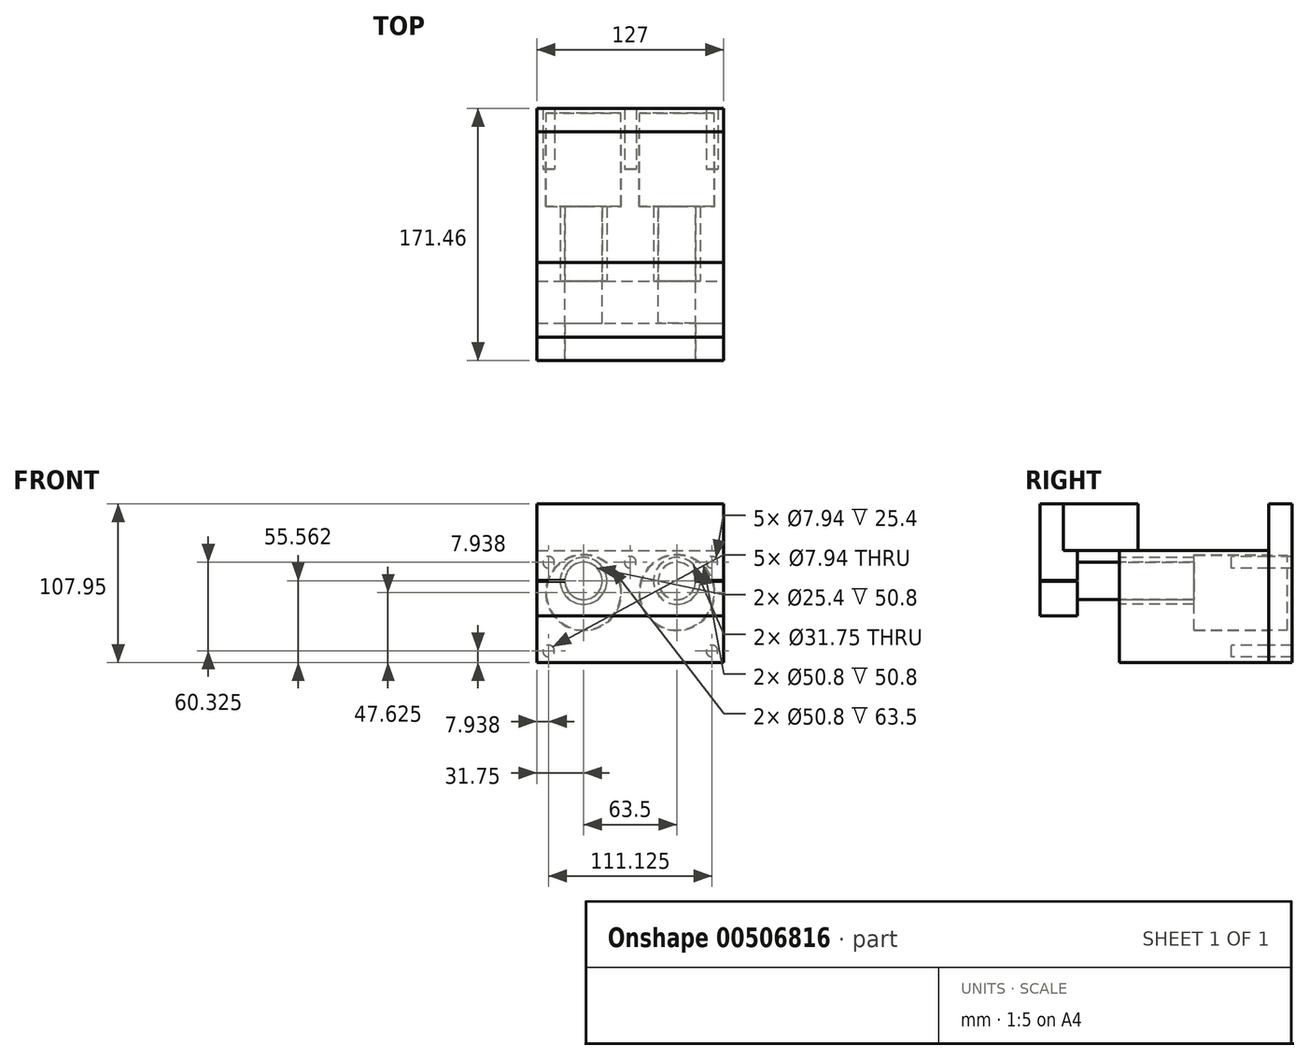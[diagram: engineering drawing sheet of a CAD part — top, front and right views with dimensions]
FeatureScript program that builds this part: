
annotation { "Feature Type Name" : "Feature", "Feature Type Description" : "" }
export const myFeature = defineFeature(function(context is Context, id is Id, definition is map)
    precondition{}
    {
        {
            var Q0;
            Q0=qCreatedBy(makeId("Front.planeOp"),FACE);
            var sketch = newSketch(context, id + "F0", { "sketchPlane" : qUnion([Q0])});
            skLineSegment(sketch, "E0.bottom", {"start": v(0, 0) * mm, "end": v(127, 0) * mm});
            skLineSegment(sketch, "E0.top", {"start": v(0, 76.2) * mm, "end": v(127, 76.2) * mm});
            skLineSegment(sketch, "E0.left", {"start": v(0, 0) * mm, "end": v(0, 76.2) * mm});
            skLineSegment(sketch, "E0.right", {"start": v(127, 0) * mm, "end": v(127, 76.2) * mm});
            skCircle(sketch, "E1", {"center": v(31.75, 47.62) * mm, "radius": 25.4 * mm});
            skCircle(sketch, "E2", {"center": v(95.25, 47.62) * mm, "radius": 25.4 * mm});
            skCircle(sketch, "E3", {"center": v(31.75, 55.56) * mm, "radius": 15.88 * mm});
            skCircle(sketch, "E4", {"center": v(95.25, 55.56) * mm, "radius": 15.88 * mm});
            skSolve(sketch);
        }
        {
            var Q0;
            Q0=makeQuery(id+"F0.imprint","IMPRINT",FACE,{"disambiguationData":[TD([[makeQuery(id+"F0.imprint","IMPRINT",EDGE,{"derivedFrom":sQuery(id+"F0.wireOp",EDGE,"E0.bottom")}),1.0]])]});
            var Q1;
            Q1=makeQuery(id+"F0.imprint","IMPRINT",FACE,{"disambiguationData":[TD([[makeQuery(id+"F0.imprint","IMPRINT",EDGE,{"derivedFrom":sQuery(id+"F0.wireOp",EDGE,"E1")}),1.0]])]});
            var Q2;
            Q2=makeQuery(id+"F0.imprint","IMPRINT",FACE,{"disambiguationData":[TD([[makeQuery(id+"F0.imprint","IMPRINT",EDGE,{"derivedFrom":sQuery(id+"F0.wireOp",EDGE,"E2")}),1.0]])]});
            extrude(context, id + "F1", {"entities" : qUnion([Q0, Q1, Q2]), "depth" : 101.6 * mm, "offsetDistance" : 25.4 * mm});
        }
        {
            var Q0;
            Q0=makeQuery(id+"F0.imprint","IMPRINT",FACE,{"disambiguationData":[TD([[makeQuery(id+"F0.imprint","IMPRINT",EDGE,{"derivedFrom":sQuery(id+"F0.wireOp",EDGE,"E1")}),1.0]])]});
            var Q1;
            Q1=makeQuery(id+"F0.imprint","IMPRINT",FACE,{"disambiguationData":[TD([[makeQuery(id+"F0.imprint","IMPRINT",EDGE,{"derivedFrom":sQuery(id+"F0.wireOp",EDGE,"E2")}),1.0]])]});
            var Q2;
            Q2=makeQuery(id+"F0.imprint","IMPRINT",FACE,{"disambiguationData":[TD([[makeQuery(id+"F0.imprint","IMPRINT",EDGE,{"derivedFrom":sQuery(id+"F0.wireOp",EDGE,"E4")}),1.0]])]});
            var Q3;
            Q3=makeQuery(id+"F0.imprint","IMPRINT",FACE,{"disambiguationData":[TD([[makeQuery(id+"F0.imprint","IMPRINT",EDGE,{"derivedFrom":sQuery(id+"F0.wireOp",EDGE,"E3")}),1.0]])]});
            extrude(context, id + "F2", {"entities" : qUnion([Q0, Q1, Q2, Q3]), "operationType" : NewBodyOperationType.REMOVE, "depth" : 50.8 * mm, "offsetDistance" : 25.4 * mm});
        }
        {
            var Q0;
            Q0=makeQuery(id+"F1.opExtrude","CAP_FACE",FACE,{"disambiguationData":[OSD([sQuery(id+"F0.wireOp",EDGE,"E0.bottom"),sQuery(id+"F0.wireOp",EDGE,"E0.top"),sQuery(id+"F0.wireOp",EDGE,"E0.left"),sQuery(id+"F0.wireOp",EDGE,"E0.right"),sQuery(id+"F0.wireOp",EDGE,"E3"),sQuery(id+"F0.wireOp",EDGE,"E4")])],"isStart":false});
            var sketch = newSketch(context, id + "F3", { "sketchPlane" : qUnion([Q0])});
            skCircle(sketch, "E5", {"center": v(31.75, 55.56) * mm, "radius": 15.88 * mm});
            skCircle(sketch, "E6", {"center": v(95.25, 55.56) * mm, "radius": 15.88 * mm});
            skCircle(sketch, "E7", {"center": v(31.75, 55.56) * mm, "radius": 12.7 * mm});
            skCircle(sketch, "E8", {"center": v(95.25, 55.56) * mm, "radius": 12.7 * mm});
            skSolve(sketch);
        }
        {
            var Q0;
            Q0 = qSketchRegion(id + "F3", true);
            extrude(context, id + "F4", {"entities" : qUnion([Q0]), "oppositeDirection" : true, "depth" : 50.8 * mm, "offsetDistance" : 25.4 * mm});
        }
        {
            var Q0;
            Q0=makeQuery(id+"F0.imprint","IMPRINT",FACE,{"disambiguationData":[TD([[makeQuery(id+"F0.imprint","IMPRINT",EDGE,{"derivedFrom":sQuery(id+"F0.wireOp",EDGE,"E0.bottom")}),1.0]])]});
            var sketch = newSketch(context, id + "F5", { "sketchPlane" : qUnion([Q0])});
            skCircle(sketch, "E9", {"center": v(95.25, 47.62) * mm, "radius": 25.4 * mm});
            skCircle(sketch, "E10", {"center": v(31.75, 47.62) * mm, "radius": 25.4 * mm});
            skCircle(sketch, "E11", {"center": v(95.25, 47.62) * mm, "radius": 25.8 * mm});
            skCircle(sketch, "E12", {"center": v(31.75, 47.62) * mm, "radius": 25.8 * mm});
            skSolve(sketch);
        }
        {
            var Q0;
            Q0 = qSketchRegion(id + "F5", true);
            extrude(context, id + "F6", {"entities" : qUnion([Q0]), "depth" : 50.8 * mm, "offsetDistance" : 25.4 * mm, "hasSecondDirection" : true, "secondDirectionOppositeDirection" : true, "secondDirectionDepth" : 12.7 * mm});
        }
        {
            var Q0;
            Q0=makeQuery(id+"F0.imprint","IMPRINT",FACE,{"disambiguationData":[TD([[makeQuery(id+"F0.imprint","IMPRINT",EDGE,{"derivedFrom":sQuery(id+"F0.wireOp",EDGE,"E0.bottom")}),1.0]])]});
            var sketch = newSketch(context, id + "F7", { "sketchPlane" : qUnion([Q0])});
            skLineSegment(sketch, "E13.bottom", {"start": v(127, 0) * mm, "end": v(0, 0) * mm});
            skLineSegment(sketch, "E13.top", {"start": v(127, 107.95) * mm, "end": v(0, 107.95) * mm});
            skLineSegment(sketch, "E13.left", {"start": v(127, 0) * mm, "end": v(127, 107.95) * mm});
            skLineSegment(sketch, "E13.right", {"start": v(0, 0) * mm, "end": v(0, 107.95) * mm});
            skCircle(sketch, "E14", {"center": v(95.25, 47.62) * mm, "radius": 25.8 * mm});
            skCircle(sketch, "E15", {"center": v(31.75, 47.62) * mm, "radius": 25.8 * mm});
            skSolve(sketch);
        }
        {
            var Q0;
            Q0 = qSketchRegion(id + "F7", true);
            extrude(context, id + "F8", {"entities" : qUnion([Q0]), "oppositeDirection" : true, "depth" : 15.88 * mm, "offsetDistance" : 25.4 * mm});
        }
        {
            var Q0;
            Q0=makeQuery(id+"F8.opExtrude","CAP_FACE",FACE,{"disambiguationData":[OSD([sQuery(id+"F7.wireOp",EDGE,"E13.bottom"),sQuery(id+"F7.wireOp",EDGE,"E13.top"),sQuery(id+"F7.wireOp",EDGE,"E13.left"),sQuery(id+"F7.wireOp",EDGE,"E13.right"),sQuery(id+"F7.wireOp",EDGE,"E14"),sQuery(id+"F7.wireOp",EDGE,"E15")])],"isStart":false});
            var sketch = newSketch(context, id + "F9", { "sketchPlane" : qUnion([Q0])});
            skCircle(sketch, "E16", {"center": v(-95.25, 47.62) * mm, "radius": 25.8 * mm});
            skCircle(sketch, "E17", {"center": v(-31.75, 47.62) * mm, "radius": 25.8 * mm});
            skSolve(sketch);
        }
        {
            var Q0;
            Q0 = qSketchRegion(id + "F9", true);
            extrude(context, id + "F10", {"entities" : qUnion([Q0]), "operationType" : NewBodyOperationType.ADD, "oppositeDirection" : true, "depth" : 3.17 * mm, "offsetDistance" : 25.4 * mm});
        }
        {
            var Q0;
            Q0=makeQuery(id+"F1.opExtrude","CAP_FACE",FACE,{"disambiguationData":[OSD([sQuery(id+"F0.wireOp",EDGE,"E0.bottom"),sQuery(id+"F0.wireOp",EDGE,"E0.top"),sQuery(id+"F0.wireOp",EDGE,"E0.left"),sQuery(id+"F0.wireOp",EDGE,"E0.right"),sQuery(id+"F0.wireOp",EDGE,"E3"),sQuery(id+"F0.wireOp",EDGE,"E4")])],"isStart":false});
            var sketch = newSketch(context, id + "F11", { "sketchPlane" : qUnion([Q0])});
            skCircle(sketch, "E18", {"center": v(31.75, 55.56) * mm, "radius": 12.7 * mm});
            skCircle(sketch, "E19", {"center": v(95.25, 55.56) * mm, "radius": 12.7 * mm});
            skSolve(sketch);
        }
        {
            var Q0;
            Q0 = qSketchRegion(id + "F11", true);
            extrude(context, id + "F12", {"entities" : qUnion([Q0]), "depth" : 53.97 * mm, "offsetDistance" : 25.4 * mm, "hasSecondDirection" : true, "secondDirectionOppositeDirection" : true, "secondDirectionDepth" : 50.8 * mm});
        }
        {
            var Q0;
            Q0=makeQuery(id+"F12.opExtrude","CAP_FACE",FACE,{"disambiguationData":[OSD([sQuery(id+"F11.wireOp",EDGE,"E18")])],"isStart":false});
            var sketch = newSketch(context, id + "F13", { "sketchPlane" : qUnion([Q0])});
            skLineSegment(sketch, "E20.bottom", {"start": v(0, 107.95) * mm, "end": v(127, 107.95) * mm});
            skLineSegment(sketch, "E20.top", {"start": v(0, 31.75) * mm, "end": v(127, 31.75) * mm});
            skLineSegment(sketch, "E20.left", {"start": v(0, 107.95) * mm, "end": v(0, 55.94) * mm});
            skLineSegment(sketch, "E20.right", {"start": v(127, 107.95) * mm, "end": v(127, 55.94) * mm});
            skArc(sketch, "E21", {"start": v(19.06, 55.18) * mm, "mid": v(44.45, 55.56) * mm, "end": v(19.06, 55.94) * mm});
            skArc(sketch, "E22", {"start": v(107.94, 55.94) * mm, "mid": v(82.55, 55.56) * mm, "end": v(107.94, 55.18) * mm});
            skLineSegment(sketch, "E23", {"start": v(0, 55.94) * mm, "end": v(19.06, 55.94) * mm});
            skLineSegment(sketch, "E24", {"start": v(0, 55.18) * mm, "end": v(19.06, 55.18) * mm});
            skLineSegment(sketch, "E25", {"start": v(107.94, 55.94) * mm, "end": v(127, 55.94) * mm});
            skPoint(sketch, "E25.endSnap0", {"position": v(127, 69.85) * mm});
            skLineSegment(sketch, "E26", {"start": v(107.94, 55.18) * mm, "end": v(127, 55.18) * mm});
            skLineSegment(sketch, "E27", {"start": v(0, 55.56) * mm, "end": v(127, 55.56) * mm, "construction": true});
            skLineSegment(sketch, "E28.trimOffspring", {"start": v(0, 55.18) * mm, "end": v(0, 31.75) * mm});
            skLineSegment(sketch, "E29.trimOffspring", {"start": v(127, 55.18) * mm, "end": v(127, 31.75) * mm});
            skLineSegment(sketch, "E30", {"start": v(0, 76.2) * mm, "end": v(127, 76.2) * mm});
            skSolve(sketch);
        }
        {
            var Q0;
            Q0 = qSketchRegion(id + "F13", true);
            extrude(context, id + "F14", {"entities" : qUnion([Q0]), "oppositeDirection" : true, "depth" : 15.88 * mm, "offsetDistance" : 25.4 * mm});
        }
        {
            var Q0;
            Q0=makeQuery(id+"F0.imprint","IMPRINT",FACE,{"disambiguationData":[TD([[makeQuery(id+"F0.imprint","IMPRINT",EDGE,{"derivedFrom":sQuery(id+"F0.wireOp",EDGE,"E0.bottom")}),1.0]])]});
            var sketch = newSketch(context, id + "F15", { "sketchPlane" : qUnion([Q0])});
            skLineSegment(sketch, "E31.bottom", {"start": v(119.06, 68.26) * mm, "end": v(7.94, 68.26) * mm, "construction": true});
            skLineSegment(sketch, "E31.top", {"start": v(119.06, 7.94) * mm, "end": v(7.94, 7.94) * mm, "construction": true});
            skLineSegment(sketch, "E31.left", {"start": v(119.06, 68.26) * mm, "end": v(119.06, 7.94) * mm, "construction": true});
            skLineSegment(sketch, "E31.right", {"start": v(7.94, 68.26) * mm, "end": v(7.94, 7.94) * mm, "construction": true});
            skCircle(sketch, "E32", {"center": v(119.06, 68.26) * mm, "radius": 3.97 * mm});
            skCircle(sketch, "E33", {"center": v(7.94, 68.26) * mm, "radius": 3.97 * mm});
            skCircle(sketch, "E34", {"center": v(119.06, 7.94) * mm, "radius": 3.97 * mm});
            skCircle(sketch, "E35", {"center": v(7.94, 7.94) * mm, "radius": 3.97 * mm});
            skCircle(sketch, "E36", {"center": v(63.5, 68.26) * mm, "radius": 3.97 * mm});
            skSolve(sketch);
        }
        {
            var Q0;
            Q0 = qSketchRegion(id + "F15", true);
            extrude(context, id + "F16", {"entities" : qUnion([Q0]), "operationType" : NewBodyOperationType.REMOVE, "oppositeDirection" : true, "depth" : 25.4 * mm, "offsetDistance" : 25.4 * mm, "hasSecondDirection" : true, "secondDirectionOppositeDirection" : false, "secondDirectionDepth" : 25.4 * mm});
        }
        {
            var Q0;
            Q0=makeQuery(id+"F13.imprint","IMPRINT",FACE,{"disambiguationData":[TD([[makeQuery(id+"F13.imprint","IMPRINT",EDGE,{"derivedFrom":sQuery(id+"F13.wireOp",EDGE,"E20.top")}),1.0]])]});
            extrude(context, id + "F17", {"entities" : qUnion([Q0]), "operationType" : NewBodyOperationType.ADD, "oppositeDirection" : true, "depth" : 25.4 * mm, "offsetDistance" : 25.4 * mm});
        }
        {
            var Q0;
            Q0=makeQuery(id+"F14.opExtrude","CAP_FACE",FACE,{"disambiguationData":[OSD([sQuery(id+"F13.wireOp",EDGE,"E20.bottom"),sQuery(id+"F13.wireOp",EDGE,"E20.top"),sQuery(id+"F13.wireOp",EDGE,"E20.left"),sQuery(id+"F13.wireOp",EDGE,"E20.right"),sQuery(id+"F13.wireOp",EDGE,"E21"),sQuery(id+"F13.wireOp",EDGE,"E22"),sQuery(id+"F13.wireOp",EDGE,"E23"),sQuery(id+"F13.wireOp",EDGE,"E24"),sQuery(id+"F13.wireOp",EDGE,"E25"),sQuery(id+"F13.wireOp",EDGE,"E26"),sQuery(id+"F13.wireOp",EDGE,"E28.trimOffspring"),sQuery(id+"F13.wireOp",EDGE,"E29.trimOffspring")])],"isStart":false});
            extrude(context, id + "F18", {"entities" : qUnion([Q0]), "depth" : 50.8 * mm, "offsetDistance" : 25.4 * mm});
        }
    });
